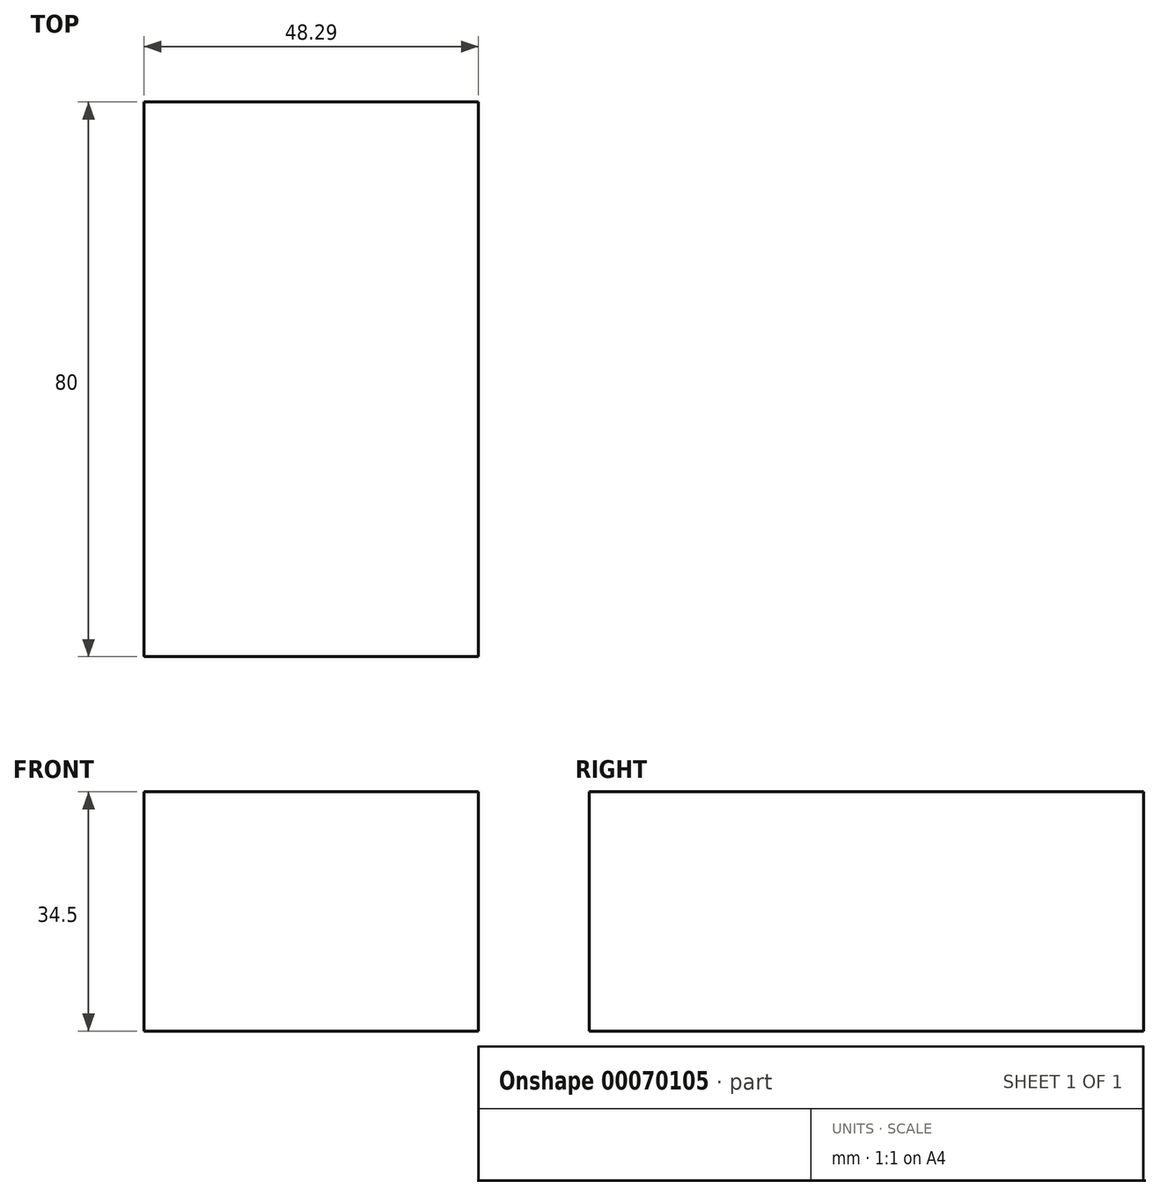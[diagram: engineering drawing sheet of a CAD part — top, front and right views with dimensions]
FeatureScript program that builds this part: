
annotation { "Feature Type Name" : "Feature", "Feature Type Description" : "" }
export const myFeature = defineFeature(function(context is Context, id is Id, definition is map)
    precondition{}
    {
        {
            var Q0;
            Q0=qCreatedBy(makeId("Front.planeOp"),FACE);
            var sketch = newSketch(context, id + "F0", { "sketchPlane" : qUnion([Q0])});
            skLineSegment(sketch, "E0.rect.bottom", {"start": v(5.43, 4.88) * mm, "end": v(-42.86, 4.88) * mm});
            skLineSegment(sketch, "E0.rect.top", {"start": v(5.43, 39.38) * mm, "end": v(-42.86, 39.38) * mm});
            skLineSegment(sketch, "E0.rect.left", {"start": v(5.43, 4.88) * mm, "end": v(5.43, 39.38) * mm});
            skLineSegment(sketch, "E0.rect.right", {"start": v(-42.86, 4.88) * mm, "end": v(-42.86, 39.38) * mm});
            skPoint(sketch, "E0.rect.middle", {"position": v(-18.72, 22.13) * mm});
            skSolve(sketch);
        }
        {
            var Q0;
            Q0 = qSketchRegion(id + "F0", true);
            extrude(context, id + "F1", {"entities" : qUnion([Q0]), "depth" : 80 * mm});
        }
    });
